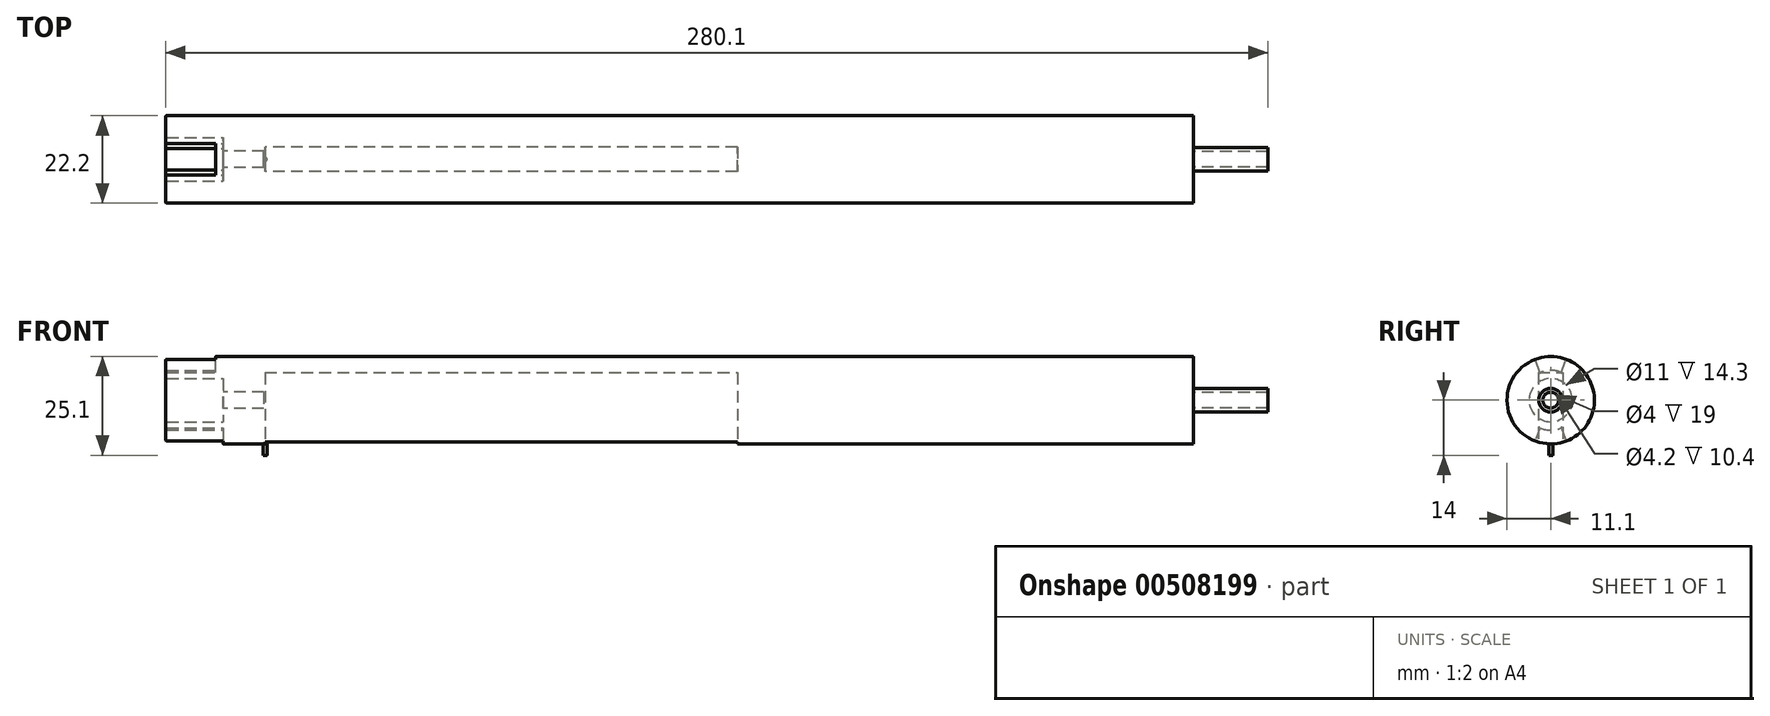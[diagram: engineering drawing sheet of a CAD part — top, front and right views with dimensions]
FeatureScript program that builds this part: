
annotation { "Feature Type Name" : "Feature", "Feature Type Description" : "" }
export const myFeature = defineFeature(function(context is Context, id is Id, definition is map)
    precondition{}
    {
        {
            var Q0;
            Q0=qCreatedBy(makeId("Right.planeOp"),FACE);
            var sketch = newSketch(context, id + "F0", { "sketchPlane" : qUnion([Q0])});
            skCircle(sketch, "E0", {"center": v(0, 14) * mm, "radius": 11.1 * mm});
            skArc(sketch, "E1", {"start": v(-2.7, 6.9) * mm, "mid": v(0, 6.4) * mm, "end": v(2.7, 6.9) * mm});
            skLineSegment(sketch, "E2", {"start": v(-2.7, 21.1) * mm, "end": v(-3.95, 24.37) * mm});
            skLineSegment(sketch, "E3", {"start": v(2.7, 21.1) * mm, "end": v(3.95, 24.37) * mm});
            skLineSegment(sketch, "E4", {"start": v(-2.7, 6.9) * mm, "end": v(-3.95, 3.63) * mm});
            skLineSegment(sketch, "E5", {"start": v(2.7, 6.9) * mm, "end": v(3.95, 3.63) * mm});
            skArc(sketch, "E6.trimOffspring", {"start": v(2.7, 21.1) * mm, "mid": v(0, 21.6) * mm, "end": v(-2.7, 21.1) * mm});
            skCircle(sketch, "E7", {"center": v(0, 14) * mm, "radius": 5.5 * mm});
            skSolve(sketch);
        }
        {
            var Q0;
            Q0=makeQuery(id+"F0.imprint","IMPRINT",FACE,{"disambiguationData":[TD([[makeQuery(id+"F0.imprint","IMPRINT",EDGE,{"derivedFrom":sQuery(id+"F0.wireOp",EDGE,"E1")}),1.0]])]});
            var Q1;
            Q1=makeQuery(id+"F0.imprint","IMPRINT",FACE,{"disambiguationData":[TD([[makeQuery(id+"F0.imprint","IMPRINT",EDGE,{"derivedFrom":sQuery(id+"F0.wireOp",EDGE,"E1")}),-1.0]])]});
            var Q2;
            {var subQ0=sQuery(id+"F0.wireOp",EDGE,"E2");Q2=makeQuery(id+"F0.imprint","IMPRINT",FACE,{"disambiguationData":[TD([[makeQuery(id+"F0.imprint","IMPRINT",EDGE,{"derivedFrom":subQ0}),-1.0]])]});}
            var Q3;
            Q3=makeQuery(id+"F0.imprint","IMPRINT",FACE,{"disambiguationData":[TD([[makeQuery(id+"F0.imprint","IMPRINT",EDGE,{"derivedFrom":sQuery(id+"F0.wireOp",EDGE,"E7")}),1.0]])]});
            extrude(context, id + "F1", {"entities" : qUnion([Q0, Q1, Q2, Q3]), "depth" : 235.8 * mm, "offsetDistance" : 25 * mm, "hasSecondDirection" : true, "secondDirectionOppositeDirection" : true, "secondDirectionDepth" : 10.7 * mm});
        }
        {
            var Q0;
            Q0=makeQuery(id+"F1.opExtrude","CAP_FACE",FACE,{"disambiguationData":[OSD([sQuery(id+"F0.wireOp",EDGE,"E0")])],"isStart":true});
            var sketch = newSketch(context, id + "F2", { "sketchPlane" : qUnion([Q0])});
            skCircle(sketch, "E8.0", {"center": v(0, 14) * mm, "radius": 11.1 * mm});
            skArc(sketch, "E8.1", {"start": v(2.7, 6.9) * mm, "mid": v(0, 6.4) * mm, "end": v(-2.7, 6.9) * mm});
            skLineSegment(sketch, "E8.2", {"start": v(2.7, 21.1) * mm, "end": v(3.95, 24.37) * mm});
            skLineSegment(sketch, "E8.3", {"start": v(-2.7, 21.1) * mm, "end": v(-3.95, 24.37) * mm});
            skLineSegment(sketch, "E8.4", {"start": v(2.7, 6.9) * mm, "end": v(3.95, 3.63) * mm});
            skLineSegment(sketch, "E8.5", {"start": v(-2.7, 6.9) * mm, "end": v(-3.95, 3.63) * mm});
            skArc(sketch, "E8.6", {"start": v(-2.7, 21.1) * mm, "mid": v(0, 21.6) * mm, "end": v(2.7, 21.1) * mm});
            skCircle(sketch, "E8.7", {"center": v(0, 14) * mm, "radius": 5.5 * mm});
            skCircle(sketch, "E8.8", {"center": v(0, 14) * mm, "radius": 11.1 * mm});
            skSolve(sketch);
        }
        {
            var Q0;
            Q0=makeQuery(id+"F2.imprint","IMPRINT",FACE,{"disambiguationData":[TD([[makeQuery(id+"F2.imprint","IMPRINT",EDGE,{"derivedFrom":sQuery(id+"F2.wireOp",EDGE,"E8.7")}),-1.0]])]});
            extrude(context, id + "F3", {"entities" : qUnion([Q0]), "operationType" : NewBodyOperationType.ADD, "depth" : 14.6 * mm, "offsetDistance" : 25 * mm});
        }
        {
            var Q0;
            {var subQ0=sQuery(id+"F2.wireOp",EDGE,"E8.2");Q0=makeQuery(id+"F2.imprint","IMPRINT",FACE,{"disambiguationData":[TD([[makeQuery(id+"F2.imprint","IMPRINT",EDGE,{"derivedFrom":subQ0}),1.0]])]});}
            var Q1;
            Q1=makeQuery(id+"F2.imprint","IMPRINT",FACE,{"disambiguationData":[TD([[makeQuery(id+"F2.imprint","IMPRINT",EDGE,{"derivedFrom":sQuery(id+"F2.wireOp",EDGE,"E8.1")}),1.0]])]});
            extrude(context, id + "F4", {"entities" : qUnion([Q0, Q1]), "operationType" : NewBodyOperationType.ADD, "depth" : 1.9 * mm, "offsetDistance" : 25 * mm});
        }
        {
            var Q0;
            Q0=makeQuery(id+"F1.opExtrude","CAP_FACE",FACE,{"disambiguationData":[OSD([sQuery(id+"F0.wireOp",EDGE,"E0")])],"isStart":false});
            var sketch = newSketch(context, id + "F5", { "sketchPlane" : qUnion([Q0])});
            skCircle(sketch, "E9", {"center": v(0, 14) * mm, "radius": 3 * mm});
            skCircle(sketch, "E10", {"center": v(0, 14) * mm, "radius": 2 * mm});
            skSolve(sketch);
        }
        {
            var Q0;
            Q0 = qSketchRegion(id + "F5", true);
            extrude(context, id + "F6", {"entities" : qUnion([Q0]), "operationType" : NewBodyOperationType.ADD, "depth" : 19 * mm, "offsetDistance" : 25 * mm});
        }
        {
            var Q0;
            Q0=makeQuery(id+"F3.opExtrude","CAP_FACE",FACE,{"disambiguationData":[OSD([sQuery(id+"F2.wireOp",EDGE,"E8.7")])],"isStart":false});
            var sketch = newSketch(context, id + "F7", { "sketchPlane" : qUnion([Q0])});
            skCircle(sketch, "E11.cCircle", {"center": v(0, 14) * mm, "radius": 5.31 * mm, "construction": true});
            skLineSegment(sketch, "E11.0", {"start": v(0, 19.31) * mm, "end": v(4.6, 16.66) * mm});
            skLineSegment(sketch, "E11.1", {"start": v(4.6, 16.66) * mm, "end": v(4.6, 11.34) * mm});
            skLineSegment(sketch, "E11.2", {"start": v(4.6, 11.34) * mm, "end": v(0, 8.69) * mm});
            skLineSegment(sketch, "E11.3", {"start": v(0, 8.69) * mm, "end": v(-4.6, 11.34) * mm});
            skLineSegment(sketch, "E11.4", {"start": v(-4.6, 11.34) * mm, "end": v(-4.6, 16.66) * mm});
            skLineSegment(sketch, "E11.5", {"start": v(-4.6, 16.66) * mm, "end": v(0, 19.31) * mm});
            skCircle(sketch, "E12", {"center": v(0, 14) * mm, "radius": 2.1 * mm});
            skSolve(sketch);
        }
        {
            var Q0;
            Q0=makeQuery(id+"F7.imprint","IMPRINT",FACE,{"disambiguationData":[TD([[makeQuery(id+"F7.imprint","IMPRINT",EDGE,{"derivedFrom":sQuery(id+"F7.wireOp",EDGE,"E12")}),1.0]])]});
            extrude(context, id + "F8", {"entities" : qUnion([Q0]), "operationType" : NewBodyOperationType.REMOVE, "oppositeDirection" : true, "depth" : 25 * mm, "offsetDistance" : 25 * mm});
        }
        {
            var Q0;
            Q0=makeQuery(id+"F7.imprint","IMPRINT",FACE,{"disambiguationData":[TD([[makeQuery(id+"F7.imprint","IMPRINT",EDGE,{"derivedFrom":sQuery(id+"F7.wireOp",EDGE,"E11.0")}),1.0]])]});
            extrude(context, id + "F9", {"entities" : qUnion([Q0]), "operationType" : NewBodyOperationType.REMOVE, "oppositeDirection" : true, "depth" : 3.3 * mm, "offsetDistance" : 25 * mm});
        }
        {
            var Q0;
            Q0=makeQuery(id+"F3.opExtrude","CAP_FACE",FACE,{"disambiguationData":[OSD([sQuery(id+"F2.wireOp",EDGE,"E8.7")])],"isStart":false});
            fillet(context, id + "F10", {"entities" : qUnion([Q0]), "tangentPropagation" : true, "radius" : 0.3 * mm, "defaultsChanged" : false, "vertexSettings" : [], "allowEdgeOverflow" : false});
        }
        {
            var Q0;
            Q0=qCreatedBy(makeId("Top.planeOp"),FACE);
            var sketch = newSketch(context, id + "F11", { "sketchPlane" : qUnion([Q0])});
            skLineSegment(sketch, "E13.bottom", {"start": v(0, -3.15) * mm, "end": v(120, -3.15) * mm});
            skLineSegment(sketch, "E13.top", {"start": v(0, 3.15) * mm, "end": v(120, 3.15) * mm});
            skLineSegment(sketch, "E13.left", {"start": v(0, -3.15) * mm, "end": v(0, 3.15) * mm});
            skLineSegment(sketch, "E13.right", {"start": v(120, -3.15) * mm, "end": v(120, 3.15) * mm});
            skPoint(sketch, "E13.middle", {"position": v(60, 0) * mm});
            skSolve(sketch);
        }
        {
            var Q0;
            Q0 = qSketchRegion(id + "F11", true);
            extrude(context, id + "F12", {"entities" : qUnion([Q0]), "operationType" : NewBodyOperationType.REMOVE, "depth" : 21 * mm, "offsetDistance" : 25 * mm});
        }
        {
            var Q0;
            Q0=qCreatedBy(makeId("Top.planeOp"),FACE);
            var sketch = newSketch(context, id + "F13", { "sketchPlane" : qUnion([Q0])});
            skCircle(sketch, "E14", {"center": v(0, 0) * mm, "radius": 0.5 * mm});
            skSolve(sketch);
        }
        {
            var Q0;
            Q0 = qSketchRegion(id + "F13", true);
            var Q1;
            {var subQ0=sQuery(id+"F2.wireOp",EDGE,"E8.8");Q1=makeQuery(id+"F4.boolean.opBoolean","MERGE",FACE,{"derivedFrom":[makeQuery(id+"F1.opExtrude","SWEPT_FACE",FACE,{"disambiguationData":[OSD([sQuery(id+"F0.wireOp",EDGE,"E0")])]}),makeQuery(id+"F4.opExtrude","SWEPT_FACE",FACE,{"disambiguationData":[OSD([subQ0]),TDD([makeQuery(id+"F2.imprint","IMPRINT",EDGE,{"disambiguationData":[TD([[makeQuery(id+"F2.imprint","INTERSECT",VERTEX,{"derivedFrom":[sQuery(id+"F2.wireOp",EDGE,"E8.2"),subQ0]}),1.0]])],"derivedFrom":subQ0})])]}),makeQuery(id+"F4.opExtrude","SWEPT_FACE",FACE,{"disambiguationData":[OSD([subQ0]),TDD([makeQuery(id+"F2.imprint","IMPRINT",EDGE,{"disambiguationData":[TD([[makeQuery(id+"F2.imprint","INTERSECT",VERTEX,{"derivedFrom":[sQuery(id+"F2.wireOp",EDGE,"E8.4"),subQ0]}),-1.0]])],"derivedFrom":subQ0})])]})]});}
            extrude(context, id + "F14", {"entities" : qUnion([Q0]), "operationType" : NewBodyOperationType.ADD, "endBound" : BoundingType.UP_TO_SURFACE, "depth" : 25 * mm, "endBoundEntityFace" : qUnion([Q1]), "offsetDistance" : 25 * mm});
        }
    });
